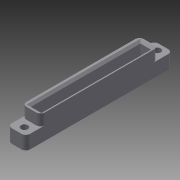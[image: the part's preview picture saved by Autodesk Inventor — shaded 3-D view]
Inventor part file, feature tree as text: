
AUTODESK INVENTOR PART (.ipt)
format: ipt  version: 2015 (Build 190159000, 159)  size: 125,952 bytes
history: native  units: in
note: dims shown in document units (in); Inventor stores cm internally (conversion verified against a paired STEP export)
features: sketch x5, extrude x4, chamfer x1
ambient origin geometry x8: Origin, YZ Plane, XZ Plane, XY Plane, X Axis, Y Axis, Z Axis, Center Point
bodies: Solid1 (feature_tree)
feature tree (10):
  extrude  "Extrusion1"  Depth=2.7228in
  extrude  "Extrusion2"  Depth=0.25in TaperAngle=0.0deg
  extrude  "Extrusion3"  Depth=0.128in
  extrude  "Extrusion4"  Depth=0.25in
  chamfer  "Chamfer1"  Distance=0.25in
  sketch  "Sketch5"  dims[d11=0.3398in d12=2.1772in d13=0.2728in d14=0.0787in d15=0.2079in d16=0.0in d17=0.1969in d18=2.0358in d19=0.4579in d20=0.0in d21=0.0394in d22=0.0787in d23=45.0deg]
  sketch  "Sketch1"  dims[d0=0.3398in d1=2.7228in]
  sketch  "Sketch2"  dims[d2=0.0787in d3=0.25in d4=0.0in]
  sketch  "Sketch3"  dims[d5=0.128in d6=0.128in]
  sketch  "Sketch4"  dims[d7=1.2344in d8=1.2344in d9=0.25in d10=0.0in]
